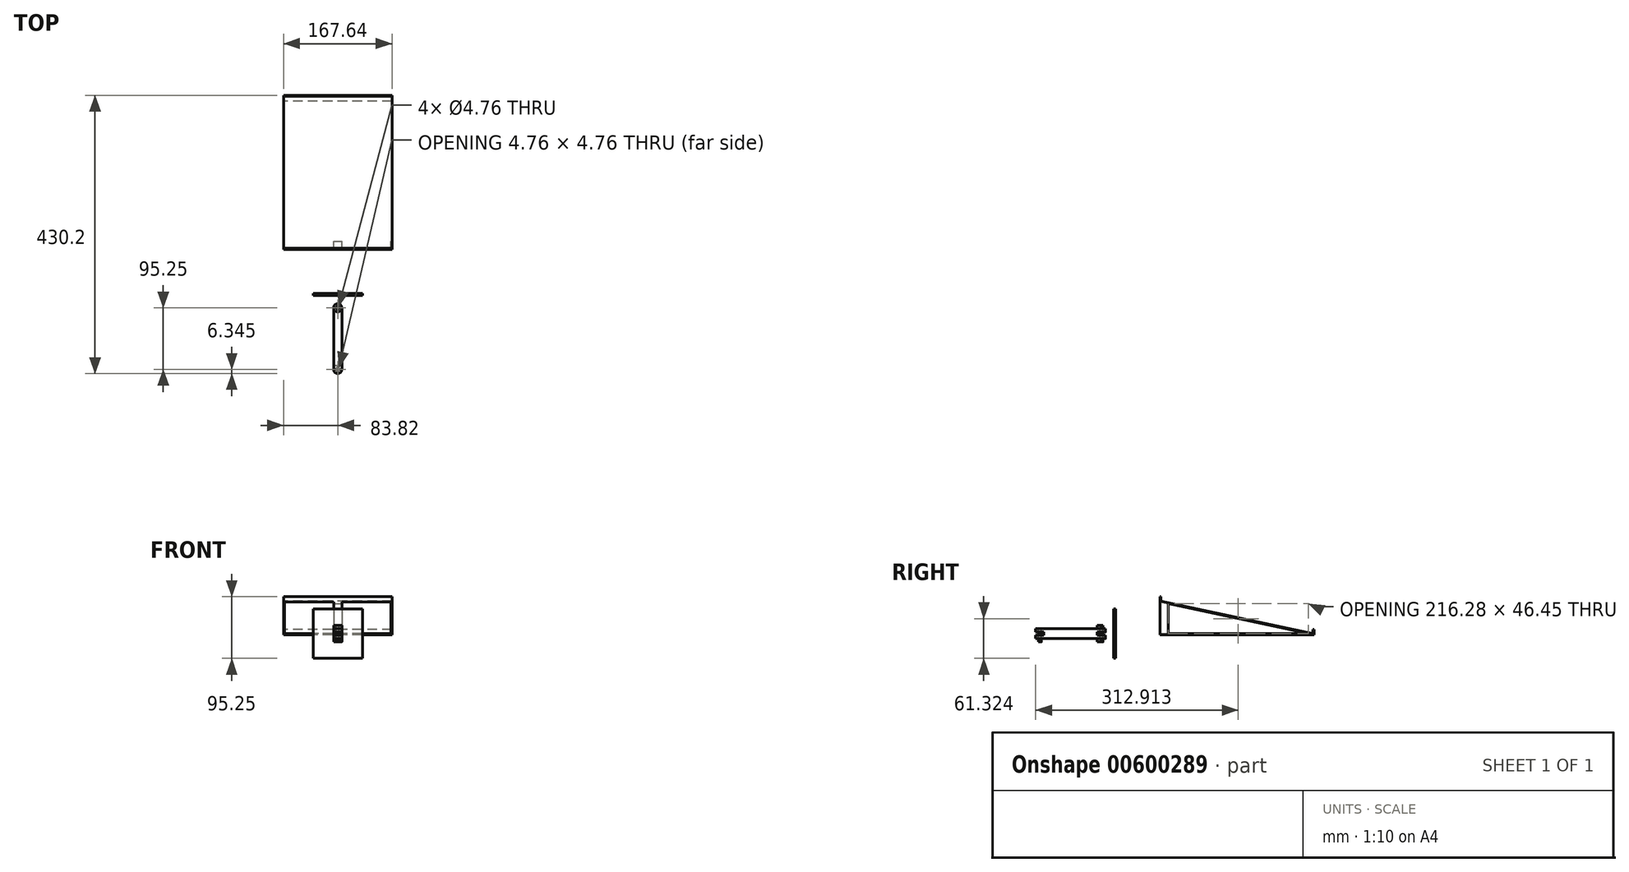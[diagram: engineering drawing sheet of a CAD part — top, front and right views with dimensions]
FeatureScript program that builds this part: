
annotation { "Feature Type Name" : "Feature", "Feature Type Description" : "" }
export const myFeature = defineFeature(function(context is Context, id is Id, definition is map)
    precondition{}
    {
        {
            var Q0;
            Q0=qCreatedBy(makeId("Front.planeOp"),FACE);
            var sketch = newSketch(context, id + "F0", { "sketchPlane" : qUnion([Q0])});
            skLineSegment(sketch, "E0.bottom", {"start": v(38.1, 38.1) * mm, "end": v(-38.1, 38.1) * mm});
            skLineSegment(sketch, "E0.top", {"start": v(38.1, -38.1) * mm, "end": v(-38.1, -38.1) * mm});
            skLineSegment(sketch, "E0.left", {"start": v(38.1, 38.1) * mm, "end": v(38.1, -38.1) * mm});
            skLineSegment(sketch, "E0.right", {"start": v(-38.1, 38.1) * mm, "end": v(-38.1, -38.1) * mm});
            skPoint(sketch, "E0.middle", {"position": v(0, 0) * mm});
            skSolve(sketch);
        }
        {
            var Q0;
            Q0 = qSketchRegion(id + "F0", true);
            extrude(context, id + "F1", {"entities" : qUnion([Q0]), "depth" : 3.17 * mm, "offsetDistance" : 25.4 * mm});
        }
        {
            var Q0;
            Q0=qCreatedBy(makeId("Top.planeOp"),FACE);
            var sketch = newSketch(context, id + "F2", { "sketchPlane" : qUnion([Q0])});
            skLineSegment(sketch, "E1.0", {"start": v(38.1, -3.18) * mm, "end": v(-38.1, -3.18) * mm});
            skLineSegment(sketch, "E2.bottom", {"start": v(-6.35, -3.18) * mm, "end": v(6.35, -3.18) * mm});
            skLineSegment(sketch, "E2.top", {"start": v(-6.35, -22.23) * mm, "end": v(6.35, -22.23) * mm});
            skLineSegment(sketch, "E2.left", {"start": v(-6.35, -3.18) * mm, "end": v(-6.35, -22.23) * mm});
            skLineSegment(sketch, "E2.right", {"start": v(6.35, -3.18) * mm, "end": v(6.35, -22.23) * mm});
            skArc(sketch, "E3", {"start": v(-6.35, -22.23) * mm, "mid": v(0, -28.58) * mm, "end": v(6.35, -22.23) * mm});
            skLineSegment(sketch, "E4", {"start": v(0, 0) * mm, "end": v(0, 9.58) * mm, "construction": true});
            skSolve(sketch);
        }
        {
            var Q0;
            Q0 = qSketchRegion(id + "F2", true);
            extrude(context, id + "F3", {"entities" : qUnion([Q0]), "depth" : 25.4 * mm, "offsetDistance" : 25.4 * mm, "symmetric" : true});
        }
        {
            var Q0;
            Q0=qCreatedBy(makeId("Right.planeOp"),FACE);
            var sketch = newSketch(context, id + "F4", { "sketchPlane" : qUnion([Q0])});
            skLineSegment(sketch, "E5", {"start": v(0, 0) * mm, "end": v(-36.37, 0) * mm, "construction": true});
            skLineSegment(sketch, "E6.bottom", {"start": v(-28.58, 2.54) * mm, "end": v(-15.88, 2.54) * mm});
            skLineSegment(sketch, "E6.top", {"start": v(-28.58, 7.62) * mm, "end": v(-15.88, 7.62) * mm});
            skLineSegment(sketch, "E6.left", {"start": v(-28.58, 2.54) * mm, "end": v(-28.58, 7.62) * mm});
            skLineSegment(sketch, "E6.right", {"start": v(-15.88, 2.54) * mm, "end": v(-15.88, 7.62) * mm});
            skPoint(sketch, "E7.0", {"position": v(-28.58, 12.7) * mm});
            skLineSegment(sketch, "E8", {"start": v(-28.58, 12.7) * mm, "end": v(-28.58, -12.73) * mm, "construction": true});
            skLineSegment(sketch, "E9.MirrorCS", {"start": v(-28.58, -2.54) * mm, "end": v(-15.88, -2.54) * mm});
            skLineSegment(sketch, "E10.MirrorCS", {"start": v(-28.58, -7.62) * mm, "end": v(-15.88, -7.62) * mm});
            skLineSegment(sketch, "E11.MirrorCS", {"start": v(-28.58, -2.54) * mm, "end": v(-28.58, -7.62) * mm});
            skLineSegment(sketch, "E12.MirrorCS", {"start": v(-15.88, -2.54) * mm, "end": v(-15.88, -7.62) * mm});
            skSolve(sketch);
        }
        {
            var Q0;
            Q0 = qSketchRegion(id + "F4", true);
            extrude(context, id + "F5", {"entities" : qUnion([Q0]), "operationType" : NewBodyOperationType.REMOVE, "endBound" : BoundingType.THROUGH_ALL, "oppositeDirection" : true, "depth" : 25.4 * mm, "offsetDistance" : 25.4 * mm, "hasSecondDirection" : true, "secondDirectionBound" : BoundingType.THROUGH_ALL, "secondDirectionOppositeDirection" : false, "secondDirectionDepth" : 25.4 * mm});
        }
        {
            var Q0;
            Q0=qCreatedBy(makeId("Top.planeOp"),FACE);
            var sketch = newSketch(context, id + "F6", { "sketchPlane" : qUnion([Q0])});
            skArc(sketch, "E13.0", {"start": v(-6.35, -22.23) * mm, "mid": v(0, -28.58) * mm, "end": v(6.35, -22.23) * mm, "construction": true});
            skArc(sketch, "E14", {"start": v(6.35, -22.23) * mm, "mid": v(0, -15.88) * mm, "end": v(-6.35, -22.23) * mm});
            skLineSegment(sketch, "E15.bottom", {"start": v(-6.35, -22.23) * mm, "end": v(6.35, -22.23) * mm});
            skLineSegment(sketch, "E15.top", {"start": v(-6.35, -41.28) * mm, "end": v(6.35, -41.28) * mm});
            skLineSegment(sketch, "E15.left", {"start": v(-6.35, -22.23) * mm, "end": v(-6.35, -41.28) * mm});
            skLineSegment(sketch, "E15.right", {"start": v(6.35, -22.23) * mm, "end": v(6.35, -41.28) * mm});
            skSolve(sketch);
        }
        {
            var Q0;
            Q0 = qSketchRegion(id + "F6", true);
            extrude(context, id + "F7", {"entities" : qUnion([Q0]), "depth" : 15.24 * mm, "offsetDistance" : 25.4 * mm, "symmetric" : true});
        }
        {
            var Q0;
            Q0=makeQuery(id+"F7.opExtrude","SWEPT_FACE",FACE,{"disambiguationData":[OSD([sQuery(id+"F6.wireOp",EDGE,"E15.right")])]});
            var sketch = newSketch(context, id + "F8", { "sketchPlane" : qUnion([Q0])});
            skLineSegment(sketch, "E16.0.0", {"start": v(-22.23, 12.7) * mm, "end": v(-22.23, 7.62) * mm});
            skLineSegment(sketch, "E16.0.1", {"start": v(-22.23, 7.62) * mm, "end": v(-15.88, 7.62) * mm});
            skLineSegment(sketch, "E16.0.2", {"start": v(-15.88, 7.62) * mm, "end": v(-15.88, 2.54) * mm});
            skLineSegment(sketch, "E16.0.3", {"start": v(-15.88, 2.54) * mm, "end": v(-22.23, 2.54) * mm});
            skLineSegment(sketch, "E16.0.4", {"start": v(-22.23, 2.54) * mm, "end": v(-22.23, -2.54) * mm});
            skLineSegment(sketch, "E16.0.5", {"start": v(-22.23, -2.54) * mm, "end": v(-15.88, -2.54) * mm});
            skLineSegment(sketch, "E16.0.6", {"start": v(-15.88, -2.54) * mm, "end": v(-15.88, -7.62) * mm});
            skLineSegment(sketch, "E16.0.7", {"start": v(-15.88, -7.62) * mm, "end": v(-22.23, -7.62) * mm});
            skLineSegment(sketch, "E16.0.8", {"start": v(-22.23, -7.62) * mm, "end": v(-22.23, -12.7) * mm});
            skLineSegment(sketch, "E16.0.9", {"start": v(-22.23, -12.7) * mm, "end": v(-3.18, -12.7) * mm});
            skLineSegment(sketch, "E16.0.10", {"start": v(-3.18, -12.7) * mm, "end": v(-3.18, 12.7) * mm});
            skLineSegment(sketch, "E16.0.11", {"start": v(-3.18, 12.7) * mm, "end": v(-22.23, 12.7) * mm});
            skLineSegment(sketch, "E17.bottom", {"start": v(-22.23, 2.54) * mm, "end": v(-28.58, 2.54) * mm});
            skLineSegment(sketch, "E17.top", {"start": v(-22.23, -2.54) * mm, "end": v(-28.58, -2.54) * mm});
            skLineSegment(sketch, "E17.right", {"start": v(-28.58, 2.54) * mm, "end": v(-28.58, -2.54) * mm});
            skLineSegment(sketch, "E18.0.0", {"start": v(-22.23, 7.62) * mm, "end": v(-28.58, 7.62) * mm});
            skLineSegment(sketch, "E18.0.1", {"start": v(-22.23, 7.62) * mm, "end": v(-22.23, 12.7) * mm});
            skLineSegment(sketch, "E18.0.2", {"start": v(-22.23, 12.7) * mm, "end": v(-28.58, 12.7) * mm});
            skSolve(sketch);
        }
        {
            var Q0;
            Q0 = qSketchRegion(id + "F8", true);
            extrude(context, id + "F9", {"entities" : qUnion([Q0]), "operationType" : NewBodyOperationType.REMOVE, "oppositeDirection" : true, "depth" : 25.4 * mm, "offsetDistance" : 25.4 * mm});
        }
        {
            var Q0;
            Q0=makeQuery(id+"F3.opExtrude","CAP_FACE",FACE,{"disambiguationData":[OSD([sQuery(id+"F2.wireOp",EDGE,"E2.bottom"),sQuery(id+"F2.wireOp",EDGE,"E2.left"),sQuery(id+"F2.wireOp",EDGE,"E2.right"),sQuery(id+"F2.wireOp",EDGE,"E3")])],"isStart":false});
            var sketch = newSketch(context, id + "F10", { "sketchPlane" : qUnion([Q0])});
            skCircle(sketch, "E19", {"center": v(0, -22.23) * mm, "radius": 2.38 * mm});
            skSolve(sketch);
        }
        {
            var Q0;
            Q0 = qSketchRegion(id + "F10", true);
            extrude(context, id + "F11", {"entities" : qUnion([Q0]), "operationType" : NewBodyOperationType.REMOVE, "endBound" : BoundingType.THROUGH_ALL, "oppositeDirection" : true, "depth" : 25.4 * mm, "offsetDistance" : 25.4 * mm});
        }
        {
            var Q0;
            Q0=makeQuery(id+"F7.opExtrude","SWEPT_FACE",FACE,{"disambiguationData":[OSD([sQuery(id+"F6.wireOp",EDGE,"E15.top")])]});
            extrude(context, id + "F12", {"entities" : qUnion([Q0]), "operationType" : NewBodyOperationType.ADD, "depth" : 76.2 * mm, "offsetDistance" : 25.4 * mm});
        }
        {
            var Q0;
            {var subQ0=sQuery(id+"F6.wireOp",EDGE,"E15.top");Q0=makeQuery(id+"F12.boolean.opBoolean","MERGE",FACE,{"derivedFrom":[makeQuery(id+"F7.opExtrude","CAP_FACE",FACE,{"disambiguationData":[OSD([sQuery(id+"F6.wireOp",EDGE,"E14"),subQ0,sQuery(id+"F6.wireOp",EDGE,"E15.left"),sQuery(id+"F6.wireOp",EDGE,"E15.right")])],"isStart":false}),makeQuery(id+"F12.opExtrude","SWEPT_FACE",FACE,{"disambiguationData":[OSD([subQ0]),TDD([makeQuery(id+"F7.opExtrude","CAP_EDGE",EDGE,{"disambiguationData":[OSD([subQ0])],"isStart":false})])]})]});}
            var sketch = newSketch(context, id + "F13", { "sketchPlane" : qUnion([Q0])});
            skArc(sketch, "E20", {"start": v(-6.35, -117.48) * mm, "mid": v(0, -123.83) * mm, "end": v(6.35, -117.48) * mm});
            skLineSegment(sketch, "E21", {"start": v(-6.35, -117.48) * mm, "end": v(6.35, -117.48) * mm});
            skSolve(sketch);
        }
        {
            var Q0;
            Q0 = qSketchRegion(id + "F13", true);
            extrude(context, id + "F14", {"entities" : qUnion([Q0]), "operationType" : NewBodyOperationType.ADD, "oppositeDirection" : true, "depth" : 15.24 * mm, "offsetDistance" : 25.4 * mm});
        }
        {
            var Q0;
            {var subQ0=sQuery(id+"F6.wireOp",EDGE,"E15.right");Q0=makeQuery(id+"F12.boolean.opBoolean","MERGE",FACE,{"derivedFrom":[makeQuery(id+"F7.opExtrude","SWEPT_FACE",FACE,{"disambiguationData":[OSD([subQ0])]}),makeQuery(id+"F12.opExtrude","SWEPT_FACE",FACE,{"disambiguationData":[OSD([sQuery(id+"F6.wireOp",EDGE,"E15.top"),subQ0])]})]});}
            var sketch = newSketch(context, id + "F15", { "sketchPlane" : qUnion([Q0])});
            skLineSegment(sketch, "E22.bottom", {"start": v(-123.83, -2.54) * mm, "end": v(-111.12, -2.54) * mm});
            skLineSegment(sketch, "E22.top", {"start": v(-123.83, 2.54) * mm, "end": v(-111.12, 2.54) * mm});
            skLineSegment(sketch, "E22.left", {"start": v(-123.83, -2.54) * mm, "end": v(-123.83, 2.54) * mm});
            skLineSegment(sketch, "E22.right", {"start": v(-111.12, -2.54) * mm, "end": v(-111.12, 2.54) * mm});
            skPoint(sketch, "E23", {"position": v(-111.12, 0) * mm});
            skLineSegment(sketch, "E24.0.0", {"start": v(-117.48, 7.62) * mm, "end": v(-123.83, 7.62) * mm, "construction": true});
            skLineSegment(sketch, "E24.0.1", {"start": v(-117.48, 7.62) * mm, "end": v(-117.48, -7.62) * mm});
            skLineSegment(sketch, "E24.0.2", {"start": v(-117.48, -7.62) * mm, "end": v(-123.83, -7.62) * mm, "construction": true});
            skLineSegment(sketch, "E24.0.3", {"start": v(-117.48, -7.62) * mm, "end": v(-117.48, 7.62) * mm, "construction": true});
            skSolve(sketch);
        }
        {
            var Q0;
            Q0 = qSketchRegion(id + "F15", true);
            var Q1;
            Q1=sQuery(id+"F15.wireOp",EDGE,"E24.0.0");
            var Q2;
            Q2=sQuery(id+"F15.wireOp",EDGE,"E24.0.3");
            var Q3;
            Q3=sQuery(id+"F15.wireOp",EDGE,"E24.0.2");
            extrude(context, id + "F16", {"entities" : qUnion([Q0]), "operationType" : NewBodyOperationType.REMOVE, "surfaceEntities" : qUnion([Q1, Q2, Q3]), "endBound" : BoundingType.THROUGH_ALL, "oppositeDirection" : true, "depth" : 25.4 * mm, "offsetDistance" : 25.4 * mm});
        }
        {
            var Q0;
            {var subQ0=sQuery(id+"F6.wireOp",EDGE,"E15.top");Q0=makeQuery(id+"F14.boolean.opBoolean","MERGE",FACE,{"derivedFrom":[makeQuery(id+"F12.boolean.opBoolean","MERGE",FACE,{"derivedFrom":[makeQuery(id+"F7.opExtrude","CAP_FACE",FACE,{"disambiguationData":[OSD([sQuery(id+"F6.wireOp",EDGE,"E14"),subQ0,sQuery(id+"F6.wireOp",EDGE,"E15.left"),sQuery(id+"F6.wireOp",EDGE,"E15.right")])],"isStart":false}),makeQuery(id+"F12.opExtrude","SWEPT_FACE",FACE,{"disambiguationData":[OSD([subQ0]),TDD([makeQuery(id+"F7.opExtrude","CAP_EDGE",EDGE,{"disambiguationData":[OSD([subQ0])],"isStart":false})])]})]}),makeQuery(id+"F14.opExtrude","CAP_FACE",FACE,{"disambiguationData":[OSD([sQuery(id+"F13.wireOp",EDGE,"E20"),sQuery(id+"F13.wireOp",EDGE,"E21")])],"isStart":true})]});}
            var sketch = newSketch(context, id + "F17", { "sketchPlane" : qUnion([Q0])});
            skCircle(sketch, "E25", {"center": v(0, -117.48) * mm, "radius": 2.38 * mm});
            skSolve(sketch);
        }
        {
            var Q0;
            Q0 = qSketchRegion(id + "F17", true);
            extrude(context, id + "F18", {"entities" : qUnion([Q0]), "operationType" : NewBodyOperationType.REMOVE, "endBound" : BoundingType.THROUGH_ALL, "oppositeDirection" : true, "depth" : 25.4 * mm, "offsetDistance" : 25.4 * mm});
        }
        {
            var Q0;
            Q0=qCreatedBy(makeId("Top.planeOp"),FACE);
            var sketch = newSketch(context, id + "F19", { "sketchPlane" : qUnion([Q0])});
            skLineSegment(sketch, "E26.bottom", {"start": v(-6.35, 68.25) * mm, "end": v(6.35, 68.25) * mm});
            skLineSegment(sketch, "E26.top", {"start": v(-6.35, 80.95) * mm, "end": v(6.35, 80.95) * mm});
            skLineSegment(sketch, "E26.left", {"start": v(-6.35, 68.25) * mm, "end": v(-6.35, 80.95) * mm});
            skLineSegment(sketch, "E26.right", {"start": v(6.35, 68.25) * mm, "end": v(6.35, 80.95) * mm});
            skPoint(sketch, "E27", {"position": v(0, 68.25) * mm});
            skSolve(sketch);
        }
        {
            var Q0;
            Q0 = qSketchRegion(id + "F19", true);
            extrude(context, id + "F20", {"entities" : qUnion([Q0]), "depth" : 50.8 * mm, "offsetDistance" : 25.4 * mm});
        }
        {
            var Q0;
            Q0=makeQuery(id+"F20.opExtrude","SWEPT_FACE",FACE,{"disambiguationData":[OSD([sQuery(id+"F19.wireOp",EDGE,"E26.right")])]});
            var sketch = newSketch(context, id + "F21", { "sketchPlane" : qUnion([Q0])});
            skLineSegment(sketch, "E28", {"start": v(68.25, 50.8) * mm, "end": v(80.95, 48.07) * mm});
            skLineSegment(sketch, "E29", {"start": v(68.25, 50.8) * mm, "end": v(304.8, 0) * mm, "construction": true});
            skLineSegment(sketch, "E30", {"start": v(68.25, 50.8) * mm, "end": v(68.25, 56.26) * mm});
            skLineSegment(sketch, "E31", {"start": v(68.25, 56.26) * mm, "end": v(81.43, 56.26) * mm});
            skLineSegment(sketch, "E32", {"start": v(81.43, 56.26) * mm, "end": v(80.95, 48.07) * mm});
            skSolve(sketch);
        }
        {
            var Q0;
            Q0 = qSketchRegion(id + "F21", true);
            extrude(context, id + "F22", {"entities" : qUnion([Q0]), "operationType" : NewBodyOperationType.REMOVE, "endBound" : BoundingType.THROUGH_ALL, "oppositeDirection" : true, "depth" : 25.4 * mm, "offsetDistance" : 25.4 * mm});
        }
        {
            var Q0;
            Q0=qCreatedBy(makeId("Right.planeOp"),FACE);
            var sketch = newSketch(context, id + "F23", { "sketchPlane" : qUnion([Q0])});
            skLineSegment(sketch, "E33.0.0", {"start": v(80.95, 48.07) * mm, "end": v(68.25, 50.8) * mm, "construction": true});
            skLineSegment(sketch, "E33.0.1", {"start": v(68.25, 50.8) * mm, "end": v(68.25, 0) * mm, "construction": true});
            skLineSegment(sketch, "E33.0.2", {"start": v(68.25, 0) * mm, "end": v(80.95, 0) * mm, "construction": true});
            skLineSegment(sketch, "E33.0.3", {"start": v(80.95, 0) * mm, "end": v(80.95, 48.07) * mm, "construction": true});
            skLineSegment(sketch, "E34", {"start": v(68.25, 0) * mm, "end": v(304.8, 0) * mm});
            skLineSegment(sketch, "E35", {"start": v(304.8, 0) * mm, "end": v(68.25, 50.8) * mm});
            skLineSegment(sketch, "E36.top", {"start": v(68.25, 57.15) * mm, "end": v(69.84, 57.15) * mm});
            skLineSegment(sketch, "E36.left", {"start": v(68.25, 49.18) * mm, "end": v(68.25, 57.15) * mm});
            skLineSegment(sketch, "E36.right", {"start": v(69.84, 50.46) * mm, "end": v(69.84, 57.15) * mm});
            skLineSegment(sketch, "E37.bottom", {"start": v(304.8, 0) * mm, "end": v(306.38, 0) * mm});
            skLineSegment(sketch, "E37.top", {"start": v(304.8, 6.35) * mm, "end": v(306.38, 6.35) * mm});
            skLineSegment(sketch, "E37.left", {"start": v(304.8, 0) * mm, "end": v(304.8, 6.35) * mm});
            skLineSegment(sketch, "E37.right", {"start": v(306.38, 0) * mm, "end": v(306.38, 6.35) * mm});
            skLineSegment(sketch, "E38.bottom", {"start": v(68.25, 0) * mm, "end": v(306.38, 0) * mm});
            skLineSegment(sketch, "E38.top", {"start": v(68.25, -1.59) * mm, "end": v(306.38, -1.59) * mm});
            skLineSegment(sketch, "E38.left", {"start": v(68.25, 0) * mm, "end": v(68.25, -1.59) * mm});
            skLineSegment(sketch, "E38.right", {"start": v(306.38, 0) * mm, "end": v(306.38, -1.59) * mm});
            skLineSegment(sketch, "E39", {"start": v(68.25, 50.8) * mm, "end": v(68.25, 49.18) * mm});
            skLineSegment(sketch, "E40", {"start": v(68.25, 49.18) * mm, "end": v(297.23, 0) * mm});
            skSolve(sketch);
        }
        {
            var Q0;
            Q0 = qSketchRegion(id + "F23", true);
            extrude(context, id + "F24", {"entities" : qUnion([Q0]), "operationType" : NewBodyOperationType.ADD, "depth" : 167.64 * mm, "offsetDistance" : 25.4 * mm, "symmetric" : true});
        }
        {
            var Q0;
            Q0=makeQuery(id+"F24.opExtrude","CAP_FACE",FACE,{"disambiguationData":[OSD([sQuery(id+"F23.wireOp",EDGE,"E35"),sQuery(id+"F23.wireOp",EDGE,"E36.top"),sQuery(id+"F23.wireOp",EDGE,"E36.left"),sQuery(id+"F23.wireOp",EDGE,"E36.right"),sQuery(id+"F23.wireOp",EDGE,"E37.top"),sQuery(id+"F23.wireOp",EDGE,"E37.left"),sQuery(id+"F23.wireOp",EDGE,"E37.right"),sQuery(id+"F23.wireOp",EDGE,"E38.bottom"),sQuery(id+"F23.wireOp",EDGE,"E38.top"),sQuery(id+"F23.wireOp",EDGE,"E38.left"),sQuery(id+"F23.wireOp",EDGE,"E38.right"),sQuery(id+"F23.wireOp",EDGE,"E39"),sQuery(id+"F23.wireOp",EDGE,"E40")])],"isStart":false});
            var sketch = newSketch(context, id + "F25", { "sketchPlane" : qUnion([Q0])});
            skLineSegment(sketch, "E41.0.0", {"start": v(80.95, 46.45) * mm, "end": v(68.25, 49.18) * mm});
            skLineSegment(sketch, "E41.0.1", {"start": v(68.25, 49.18) * mm, "end": v(68.25, 0) * mm});
            skLineSegment(sketch, "E41.0.2", {"start": v(68.25, 0) * mm, "end": v(80.95, 0) * mm});
            skLineSegment(sketch, "E41.0.3", {"start": v(80.95, 0) * mm, "end": v(80.95, 46.45) * mm});
            skSolve(sketch);
        }
        {
            var Q0;
            Q0 = qSketchRegion(id + "F25", true);
            extrude(context, id + "F26", {"entities" : qUnion([Q0]), "operationType" : NewBodyOperationType.ADD, "oppositeDirection" : true, "depth" : 1.59 * mm, "offsetDistance" : 25.4 * mm});
        }
        {
            var Q0;
            Q0=makeQuery(id+"F24.opExtrude","CAP_FACE",FACE,{"disambiguationData":[OSD([sQuery(id+"F23.wireOp",EDGE,"E35"),sQuery(id+"F23.wireOp",EDGE,"E36.top"),sQuery(id+"F23.wireOp",EDGE,"E36.left"),sQuery(id+"F23.wireOp",EDGE,"E36.right"),sQuery(id+"F23.wireOp",EDGE,"E37.top"),sQuery(id+"F23.wireOp",EDGE,"E37.left"),sQuery(id+"F23.wireOp",EDGE,"E37.right"),sQuery(id+"F23.wireOp",EDGE,"E38.bottom"),sQuery(id+"F23.wireOp",EDGE,"E38.top"),sQuery(id+"F23.wireOp",EDGE,"E38.left"),sQuery(id+"F23.wireOp",EDGE,"E38.right"),sQuery(id+"F23.wireOp",EDGE,"E39"),sQuery(id+"F23.wireOp",EDGE,"E40")])],"isStart":true});
            var sketch = newSketch(context, id + "F27", { "sketchPlane" : qUnion([Q0])});
            skLineSegment(sketch, "E42.0.0", {"start": v(-68.25, 0) * mm, "end": v(-68.25, 49.18) * mm});
            skLineSegment(sketch, "E42.0.1", {"start": v(-68.25, 49.18) * mm, "end": v(-80.95, 46.45) * mm});
            skLineSegment(sketch, "E42.0.2", {"start": v(-80.95, 46.45) * mm, "end": v(-80.95, 0) * mm});
            skLineSegment(sketch, "E42.0.3", {"start": v(-80.95, 0) * mm, "end": v(-68.25, 0) * mm});
            skSolve(sketch);
        }
        {
            var Q0;
            Q0 = qSketchRegion(id + "F27", true);
            extrude(context, id + "F28", {"entities" : qUnion([Q0]), "operationType" : NewBodyOperationType.ADD, "oppositeDirection" : true, "depth" : 1.59 * mm, "offsetDistance" : 25.4 * mm});
        }
        {
            var Q0;
            Q0=makeQuery(id+"F3.opExtrude","CAP_FACE",FACE,{"disambiguationData":[OSD([sQuery(id+"F2.wireOp",EDGE,"E2.bottom"),sQuery(id+"F2.wireOp",EDGE,"E2.left"),sQuery(id+"F2.wireOp",EDGE,"E2.right"),sQuery(id+"F2.wireOp",EDGE,"E3")])],"isStart":false});
            var sketch = newSketch(context, id + "F29", { "sketchPlane" : qUnion([Q0])});
            skCircle(sketch, "E43.0", {"center": v(0, -22.23) * mm, "radius": 2.38 * mm});
            skSolve(sketch);
        }
        {
            var Q0;
            Q0 = qSketchRegion(id + "F29", true);
            extrude(context, id + "F30", {"entities" : qUnion([Q0]), "oppositeDirection" : true, "depth" : 25.4 * mm, "offsetDistance" : 25.4 * mm});
        }
        {
            var Q0;
            {var subQ0=sQuery(id+"F6.wireOp",EDGE,"E15.top");Q0=makeQuery(id+"F14.boolean.opBoolean","MERGE",FACE,{"derivedFrom":[makeQuery(id+"F12.boolean.opBoolean","MERGE",FACE,{"derivedFrom":[makeQuery(id+"F7.opExtrude","CAP_FACE",FACE,{"disambiguationData":[OSD([sQuery(id+"F6.wireOp",EDGE,"E14"),subQ0,sQuery(id+"F6.wireOp",EDGE,"E15.left"),sQuery(id+"F6.wireOp",EDGE,"E15.right")])],"isStart":false}),makeQuery(id+"F12.opExtrude","SWEPT_FACE",FACE,{"disambiguationData":[OSD([subQ0]),TDD([makeQuery(id+"F7.opExtrude","CAP_EDGE",EDGE,{"disambiguationData":[OSD([subQ0])],"isStart":false})])]})]}),makeQuery(id+"F14.opExtrude","CAP_FACE",FACE,{"disambiguationData":[OSD([sQuery(id+"F13.wireOp",EDGE,"E20"),sQuery(id+"F13.wireOp",EDGE,"E21")])],"isStart":true})]});}
            var sketch = newSketch(context, id + "F31", { "sketchPlane" : qUnion([Q0])});
            skCircle(sketch, "E44.0", {"center": v(0, -117.48) * mm, "radius": 2.38 * mm});
            skSolve(sketch);
        }
        {
            var Q0;
            Q0 = qSketchRegion(id + "F31", true);
            extrude(context, id + "F32", {"entities" : qUnion([Q0]), "oppositeDirection" : true, "depth" : 20.32 * mm, "offsetDistance" : 25.4 * mm});
        }
    });
